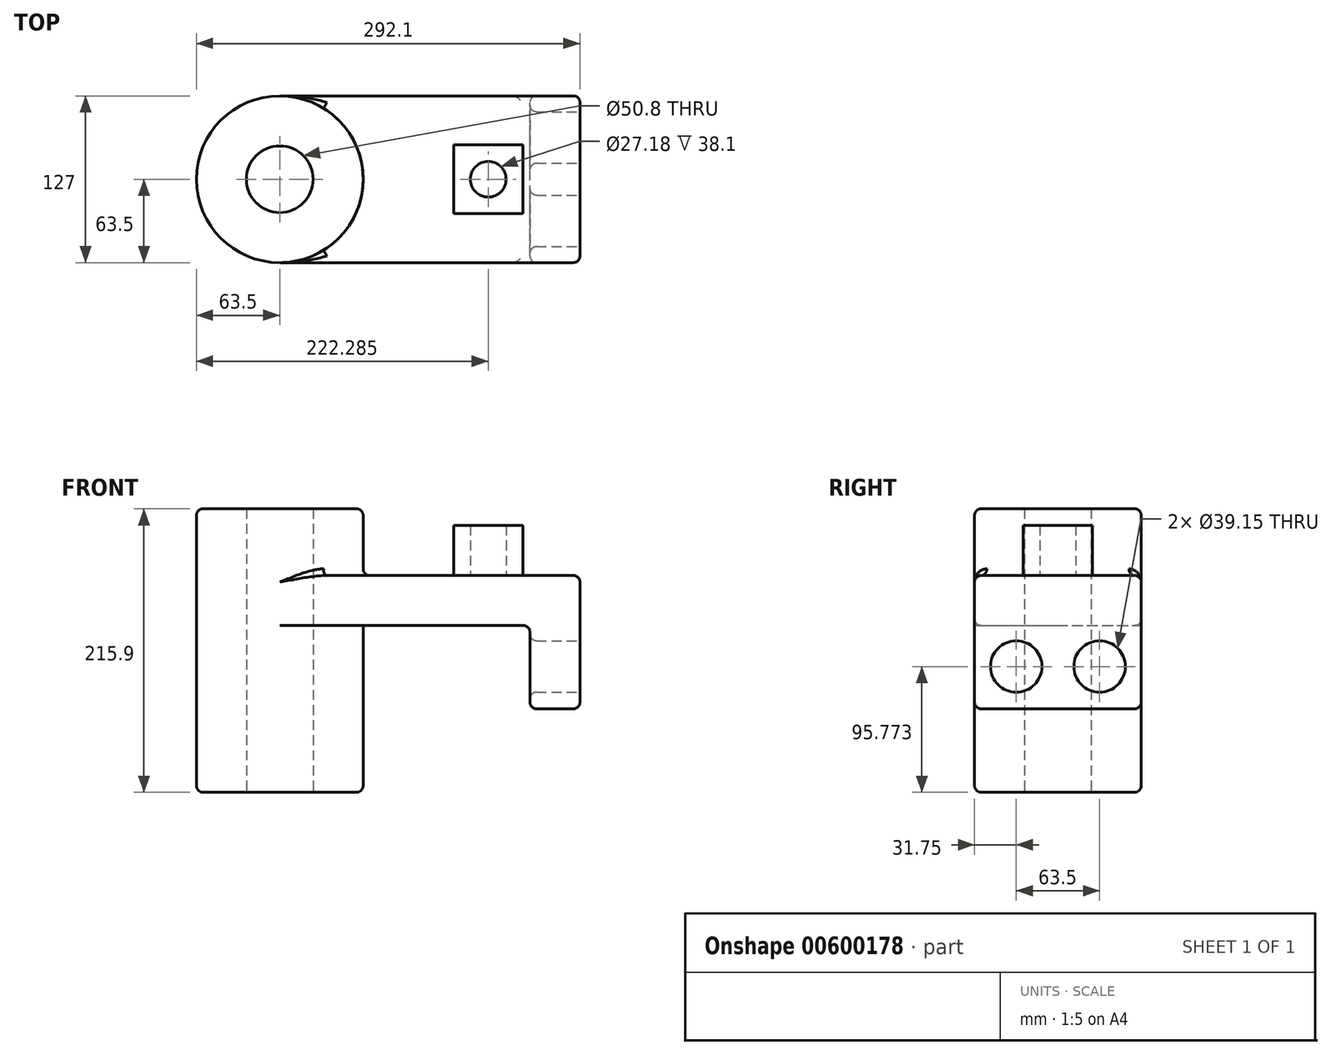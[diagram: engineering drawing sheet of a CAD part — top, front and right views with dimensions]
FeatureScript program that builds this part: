
annotation { "Feature Type Name" : "Feature", "Feature Type Description" : "" }
export const myFeature = defineFeature(function(context is Context, id is Id, definition is map)
    precondition{}
    {
        {
            var Q0;
            Q0=qCreatedBy(makeId("Top.planeOp"),FACE);
            var sketch = newSketch(context, id + "F0", { "sketchPlane" : qUnion([Q0])});
            skLineSegment(sketch, "E0.bottom", {"start": v(-114.3, -63.5) * mm, "end": v(114.3, -63.5) * mm});
            skLineSegment(sketch, "E0.top", {"start": v(-114.3, 63.5) * mm, "end": v(114.3, 63.5) * mm});
            skLineSegment(sketch, "E0.left", {"start": v(-114.3, -63.5) * mm, "end": v(-114.3, 63.5) * mm});
            skLineSegment(sketch, "E0.right", {"start": v(114.3, -63.5) * mm, "end": v(114.3, 63.5) * mm});
            skPoint(sketch, "E0.middle", {"position": v(0, 0) * mm});
            skCircle(sketch, "E1", {"center": v(-114.3, 0) * mm, "radius": 63.5 * mm});
            skCircle(sketch, "E2", {"center": v(-114.3, 0) * mm, "radius": 25.4 * mm});
            skSolve(sketch);
        }
        {
            var Q0;
            {var subQ1=sQuery(id+"F0.wireOp",EDGE,"E0.left");var subQ3=sQuery(id+"F0.wireOp",EDGE,"E2");var subQ4=makeQuery(id+"F0.imprint","INTERSECT",VERTEX,{"disambiguationData":[OD(0.0)],"derivedFrom":[subQ1,subQ3]});Q0=makeQuery(id+"F0.imprint","IMPRINT",FACE,{"disambiguationData":[TD([[makeQuery(id+"F0.imprint","IMPRINT",EDGE,{"disambiguationData":[TD([[subQ4,1.0]])],"derivedFrom":subQ3}),-1.0]])]});}
            var Q1;
            {var subQ1=sQuery(id+"F0.wireOp",EDGE,"E0.left");var subQ3=sQuery(id+"F0.wireOp",EDGE,"E2");var subQ4=makeQuery(id+"F0.imprint","INTERSECT",VERTEX,{"disambiguationData":[OD(0.0)],"derivedFrom":[subQ1,subQ3]});Q1=makeQuery(id+"F0.imprint","IMPRINT",FACE,{"disambiguationData":[TD([[makeQuery(id+"F0.imprint","IMPRINT",EDGE,{"disambiguationData":[TD([[subQ4,-1.0]])],"derivedFrom":subQ3}),-1.0]])]});}
            var Q2;
            {var subQ0=sQuery(id+"F0.wireOp",EDGE,"E0.bottom");Q2=makeQuery(id+"F0.imprint","IMPRINT",FACE,{"disambiguationData":[TD([[makeQuery(id+"F0.imprint","IMPRINT",EDGE,{"derivedFrom":subQ0}),1.0]])]});}
            extrude(context, id + "F1", {"entities" : qUnion([Q0, Q1, Q2]), "depth" : 38.1 * mm, "offsetDistance" : 25.4 * mm});
        }
        {
            var Q0;
            Q0=makeQuery(id+"F1.opExtrude","SWEPT_FACE",FACE,{"disambiguationData":[OSD([sQuery(id+"F0.wireOp",EDGE,"E0.right")])]});
            var sketch = newSketch(context, id + "F2", { "sketchPlane" : qUnion([Q0])});
            skLineSegment(sketch, "E3.bottom", {"start": v(-63.5, 38.1) * mm, "end": v(63.5, 38.1) * mm});
            skLineSegment(sketch, "E3.top", {"start": v(-63.5, -63.5) * mm, "end": v(63.5, -63.5) * mm});
            skLineSegment(sketch, "E3.left", {"start": v(-63.5, 38.1) * mm, "end": v(-63.5, -63.5) * mm});
            skLineSegment(sketch, "E3.right", {"start": v(63.5, 38.1) * mm, "end": v(63.5, -63.5) * mm});
            skCircle(sketch, "E4", {"center": v(-31.75, -31.23) * mm, "radius": 19.57 * mm});
            skLineSegment(sketch, "E5", {"start": v(0, 0) * mm, "end": v(0, -63.5) * mm, "construction": true});
            skCircle(sketch, "E6.MirrorC", {"center": v(31.75, -31.23) * mm, "radius": 19.57 * mm});
            skSolve(sketch);
        }
        {
            var Q0;
            {var subQ2=sQuery(id+"F2.wireOp",EDGE,"E3.top");Q0=makeQuery(id+"F2.imprint","IMPRINT",FACE,{"disambiguationData":[TD([[makeQuery(id+"F2.imprint","IMPRINT",EDGE,{"derivedFrom":subQ2}),1.0]])]});}
            extrude(context, id + "F3", {"entities" : qUnion([Q0]), "operationType" : NewBodyOperationType.ADD, "oppositeDirection" : true, "depth" : 38.1 * mm, "offsetDistance" : 25.4 * mm});
        }
        {
            var Q0;
            {var subQ1=sQuery(id+"F0.wireOp",EDGE,"E0.left");var subQ3=sQuery(id+"F0.wireOp",EDGE,"E2");var subQ4=makeQuery(id+"F0.imprint","INTERSECT",VERTEX,{"disambiguationData":[OD(0.0)],"derivedFrom":[subQ1,subQ3]});Q0=makeQuery(id+"F0.imprint","IMPRINT",FACE,{"disambiguationData":[TD([[makeQuery(id+"F0.imprint","IMPRINT",EDGE,{"disambiguationData":[TD([[subQ4,1.0]])],"derivedFrom":subQ3}),-1.0]])]});}
            var Q1;
            {var subQ1=sQuery(id+"F0.wireOp",EDGE,"E0.left");var subQ3=sQuery(id+"F0.wireOp",EDGE,"E2");var subQ4=makeQuery(id+"F0.imprint","INTERSECT",VERTEX,{"disambiguationData":[OD(0.0)],"derivedFrom":[subQ1,subQ3]});Q1=makeQuery(id+"F0.imprint","IMPRINT",FACE,{"disambiguationData":[TD([[makeQuery(id+"F0.imprint","IMPRINT",EDGE,{"disambiguationData":[TD([[subQ4,-1.0]])],"derivedFrom":subQ3}),-1.0]])]});}
            extrude(context, id + "F4", {"entities" : qUnion([Q0, Q1]), "operationType" : NewBodyOperationType.ADD, "depth" : 88.9 * mm, "offsetDistance" : 25.4 * mm});
        }
        {
            var Q0;
            Q0=makeQuery(id+"F1.opExtrude","CAP_EDGE",EDGE,{"disambiguationData":[OSD([sQuery(id+"F0.wireOp",EDGE,"E0.bottom")])],"isStart":false});
            var Q1;
            Q1=makeQuery(id+"F1.opExtrude","CAP_EDGE",EDGE,{"disambiguationData":[OSD([sQuery(id+"F0.wireOp",EDGE,"E0.right")])],"isStart":false});
            var Q2;
            Q2=makeQuery(id+"F1.opExtrude","CAP_EDGE",EDGE,{"disambiguationData":[OSD([sQuery(id+"F0.wireOp",EDGE,"E0.top")])],"isStart":false});
            var Q3;
            Q3=makeQuery(id+"F3.opExtrude","CAP_FACE",FACE,{"disambiguationData":[OSD([sQuery(id+"F0.wireOp",EDGE,"E0.right"),sQuery(id+"F2.wireOp",EDGE,"E3.top"),sQuery(id+"F2.wireOp",EDGE,"E3.left"),sQuery(id+"F2.wireOp",EDGE,"E3.right"),sQuery(id+"F2.wireOp",EDGE,"E4"),sQuery(id+"F2.wireOp",EDGE,"E6.MirrorC")])],"isStart":false});
            var Q4;
            Q4=makeQuery(id+"F3.opExtrude","CAP_EDGE",EDGE,{"disambiguationData":[OSD([sQuery(id+"F2.wireOp",EDGE,"E3.top")])],"isStart":true});
            var Q5;
            Q5=makeQuery(id+"F3.boolean.opBoolean","MERGE",EDGE,{"derivedFrom":[makeQuery(id+"F1.opExtrude","SWEPT_EDGE",EDGE,{"disambiguationData":[OSD([sQuery(id+"F0.wireOp",EDGE,"E0.bottom"),sQuery(id+"F0.wireOp",EDGE,"E0.right")])]}),makeQuery(id+"F3.opExtrude","CAP_EDGE",EDGE,{"disambiguationData":[OSD([sQuery(id+"F2.wireOp",EDGE,"E3.left")])],"isStart":true})]});
            var Q6;
            Q6=makeQuery(id+"F3.boolean.opBoolean","MERGE",EDGE,{"derivedFrom":[makeQuery(id+"F1.opExtrude","SWEPT_EDGE",EDGE,{"disambiguationData":[OSD([sQuery(id+"F0.wireOp",EDGE,"E0.top"),sQuery(id+"F0.wireOp",EDGE,"E0.right")])]}),makeQuery(id+"F3.opExtrude","CAP_EDGE",EDGE,{"disambiguationData":[OSD([sQuery(id+"F2.wireOp",EDGE,"E3.right")])],"isStart":true})]});
            var Q7;
            {var subQ0=sQuery(id+"F0.wireOp",EDGE,"E1");Q7=makeQuery(id+"F4.boolean.opBoolean","INTERSECT",EDGE,{"derivedFrom":[makeQuery(id+"F1.opExtrude","CAP_FACE",FACE,{"disambiguationData":[OSD([sQuery(id+"F0.wireOp",EDGE,"E0.bottom"),sQuery(id+"F0.wireOp",EDGE,"E0.top"),sQuery(id+"F0.wireOp",EDGE,"E0.right"),subQ0,sQuery(id+"F0.wireOp",EDGE,"E2")])],"isStart":false}),makeQuery(id+"F4.opExtrude","SWEPT_FACE",FACE,{"disambiguationData":[OSD([subQ0])]})]});}
            var Q8;
            Q8=makeQuery(id+"F4.opExtrude","CAP_EDGE",EDGE,{"disambiguationData":[OSD([sQuery(id+"F0.wireOp",EDGE,"E1")])],"isStart":false});
            var Q9;
            Q9=makeQuery(id+"F3.opExtrude","SWEPT_EDGE",EDGE,{"disambiguationData":[OSD([sQuery(id+"F2.wireOp",EDGE,"E3.top"),sQuery(id+"F2.wireOp",EDGE,"E3.left")])]});
            var Q10;
            Q10=makeQuery(id+"F3.opExtrude","SWEPT_EDGE",EDGE,{"disambiguationData":[OSD([sQuery(id+"F2.wireOp",EDGE,"E3.top"),sQuery(id+"F2.wireOp",EDGE,"E3.right")])]});
            fillet(context, id + "F5", {"entities" : qUnion([Q0, Q1, Q2, Q3, Q4, Q5, Q6, Q7, Q8, Q9, Q10]), "radius" : 5.08 * mm, "tangentPropagation" : true, "allowEdgeOverflow" : false});
        }
        {
            var Q0;
            {var subQ1=sQuery(id+"F0.wireOp",EDGE,"E0.left");var subQ3=sQuery(id+"F0.wireOp",EDGE,"E2");var subQ4=makeQuery(id+"F0.imprint","INTERSECT",VERTEX,{"disambiguationData":[OD(0.0)],"derivedFrom":[subQ1,subQ3]});Q0=makeQuery(id+"F0.imprint","IMPRINT",FACE,{"disambiguationData":[TD([[makeQuery(id+"F0.imprint","IMPRINT",EDGE,{"disambiguationData":[TD([[subQ4,1.0]])],"derivedFrom":subQ3}),-1.0]])]});}
            var Q1;
            {var subQ1=sQuery(id+"F0.wireOp",EDGE,"E0.left");var subQ3=sQuery(id+"F0.wireOp",EDGE,"E2");var subQ4=makeQuery(id+"F0.imprint","INTERSECT",VERTEX,{"disambiguationData":[OD(0.0)],"derivedFrom":[subQ1,subQ3]});Q1=makeQuery(id+"F0.imprint","IMPRINT",FACE,{"disambiguationData":[TD([[makeQuery(id+"F0.imprint","IMPRINT",EDGE,{"disambiguationData":[TD([[subQ4,-1.0]])],"derivedFrom":subQ3}),-1.0]])]});}
            extrude(context, id + "F6", {"entities" : qUnion([Q0, Q1]), "operationType" : NewBodyOperationType.ADD, "oppositeDirection" : true, "depth" : 127 * mm, "offsetDistance" : 25.4 * mm});
        }
        {
            var Q0;
            Q0=makeQuery(id+"F6.opExtrude","CAP_EDGE",EDGE,{"disambiguationData":[OSD([sQuery(id+"F0.wireOp",EDGE,"E1")])],"isStart":false});
            fillet(context, id + "F7", {"entities" : qUnion([Q0]), "radius" : 5.08 * mm, "tangentPropagation" : true, "allowEdgeOverflow" : false});
        }
        {
            var Q0;
            Q0=makeQuery(id+"F1.opExtrude","CAP_FACE",FACE,{"disambiguationData":[OSD([sQuery(id+"F0.wireOp",EDGE,"E0.bottom"),sQuery(id+"F0.wireOp",EDGE,"E0.top"),sQuery(id+"F0.wireOp",EDGE,"E0.right"),sQuery(id+"F0.wireOp",EDGE,"E1"),sQuery(id+"F0.wireOp",EDGE,"E2")])],"isStart":false});
            var sketch = newSketch(context, id + "F8", { "sketchPlane" : qUnion([Q0])});
            skLineSegment(sketch, "E7.bottom", {"start": v(18.2, -26.29) * mm, "end": v(70.77, -26.29) * mm});
            skLineSegment(sketch, "E7.top", {"start": v(18.2, 26.29) * mm, "end": v(70.77, 26.29) * mm});
            skLineSegment(sketch, "E7.left", {"start": v(18.2, -26.29) * mm, "end": v(18.2, 26.29) * mm});
            skLineSegment(sketch, "E7.right", {"start": v(70.77, -26.29) * mm, "end": v(70.77, 26.29) * mm});
            skCircle(sketch, "E8", {"center": v(44.49, 0) * mm, "radius": 13.59 * mm});
            skSolve(sketch);
        }
        {
            var Q0;
            Q0 = qSketchRegion(id + "F8", true);
            extrude(context, id + "F9", {"entities" : qUnion([Q0]), "operationType" : NewBodyOperationType.ADD, "depth" : 38.1 * mm, "offsetDistance" : 25.4 * mm});
        }
    });
